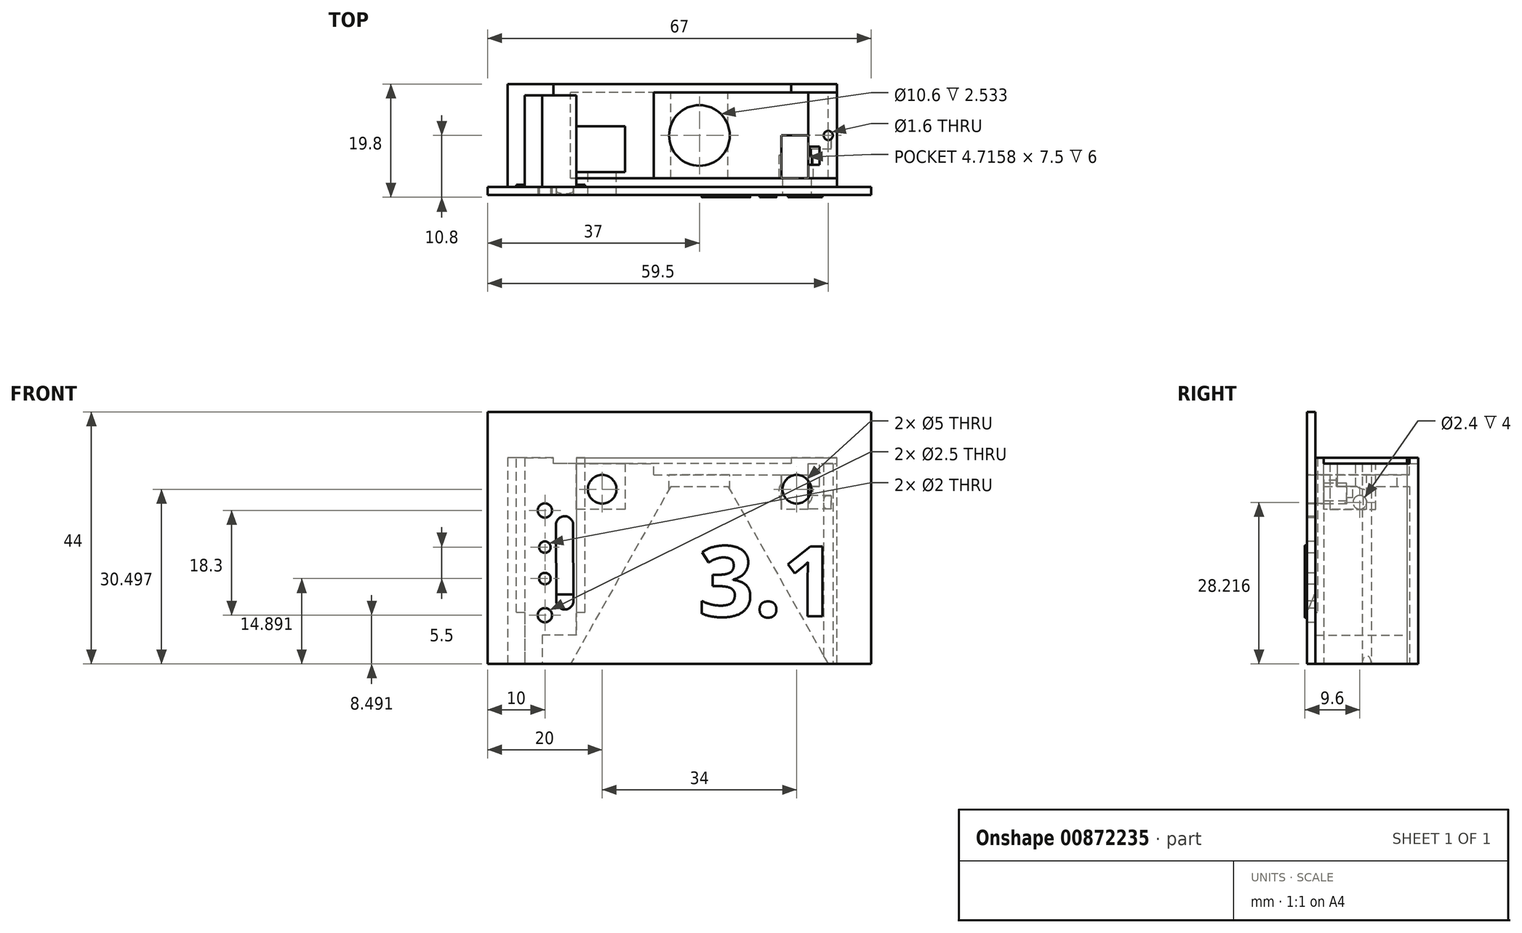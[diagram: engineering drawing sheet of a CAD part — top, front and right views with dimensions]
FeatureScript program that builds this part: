
annotation { "Feature Type Name" : "Feature", "Feature Type Description" : "" }
export const myFeature = defineFeature(function(context is Context, id is Id, definition is map)
    precondition{}
    {
        {
            var Q0;
            Q0=qCreatedBy(makeId("Front.planeOp"),FACE);
            var sketch = newSketch(context, id + "F0", { "sketchPlane" : qUnion([Q0])});
            skLineSegment(sketch, "E0", {"start": v(-6.5, 28.2) * mm, "end": v(6.5, 28.2) * mm});
            skLineSegment(sketch, "E1", {"start": v(-5, 24.2) * mm, "end": v(-22.5, -6.8) * mm});
            skLineSegment(sketch, "E2", {"start": v(5, 24.2) * mm, "end": v(22.5, -6.8) * mm});
            skLineSegment(sketch, "E3", {"start": v(-5, 24.2) * mm, "end": v(5, 24.2) * mm});
            skLineSegment(sketch, "E4", {"start": v(6.5, 24.2) * mm, "end": v(24, -6.8) * mm});
            skLineSegment(sketch, "E5", {"start": v(-24, -6.8) * mm, "end": v(-6.5, 24.2) * mm});
            skLineSegment(sketch, "E6", {"start": v(-24, -6.8) * mm, "end": v(-22.5, -6.8) * mm});
            skLineSegment(sketch, "E7.trimOffspring", {"start": v(22.5, -6.8) * mm, "end": v(24, -6.8) * mm});
            skPoint(sketch, "E8.orphan", {"position": v(-13.41, 24.2) * mm});
            skLineSegment(sketch, "E9", {"start": v(-6.5, 24.2) * mm, "end": v(-6.5, 28.2) * mm});
            skLineSegment(sketch, "E10", {"start": v(6.5, 24.2) * mm, "end": v(6.5, 28.2) * mm});
            skPoint(sketch, "E11.orphan", {"position": v(-7, 28.2) * mm});
            skSolve(sketch);
        }
        {
            var Q0;
            Q0 = qSketchRegion(id + "F0", true);
            extrude(context, id + "F1", {"entities" : qUnion([Q0]), "depth" : 15 * mm, "offsetDistance" : 25 * mm});
        }
        {
            var Q0;
            Q0=makeQuery(id+"F1.opExtrude","SWEPT_FACE",FACE,{"disambiguationData":[OSD([sQuery(id+"F0.wireOp",EDGE,"E9")])]});
            var sketch = newSketch(context, id + "F2", { "sketchPlane" : qUnion([Q0])});
            skLineSegment(sketch, "E12", {"start": v(0, 28.2) * mm, "end": v(15, 28.2) * mm});
            skLineSegment(sketch, "E13", {"start": v(15, 28.2) * mm, "end": v(15, 24.2) * mm});
            skLineSegment(sketch, "E14", {"start": v(15, 24.2) * mm, "end": v(0, 24.2) * mm});
            skLineSegment(sketch, "E15", {"start": v(0, 24.2) * mm, "end": v(0, 28.2) * mm});
            skSolve(sketch);
        }
        {
            var Q0;
            Q0 = qSketchRegion(id + "F2", true);
            extrude(context, id + "F3", {"entities" : qUnion([Q0]), "operationType" : NewBodyOperationType.ADD, "oppositeDirection" : true, "depth" : 25 * mm, "offsetDistance" : 25 * mm, "hasSecondDirection" : true, "secondDirectionOppositeDirection" : false, "secondDirectionDepth" : 1 * mm});
        }
        {
            var Q0;
            Q0=makeQuery(id+"F3.boolean.opBoolean","MERGE",FACE,{"derivedFrom":[makeQuery(id+"F1.opExtrude","SWEPT_FACE",FACE,{"disambiguationData":[OSD([sQuery(id+"F0.wireOp",EDGE,"E0")])]}),makeQuery(id+"F3.opExtrude","SWEPT_FACE",FACE,{"disambiguationData":[OSD([sQuery(id+"F2.wireOp",EDGE,"E12")])]})]});
            var sketch = newSketch(context, id + "F4", { "sketchPlane" : qUnion([Q0])});
            skLineSegment(sketch, "E16", {"start": v(-7.5, -7.5) * mm, "end": v(30.98, -7.5) * mm});
            skCircle(sketch, "E17", {"center": v(0, -7.5) * mm, "radius": 5.3 * mm});
            skSolve(sketch);
        }
        {
            var Q0;
            Q0=makeQuery(id+"F3.boolean.opBoolean","MERGE",FACE,{"derivedFrom":[makeQuery(id+"F1.opExtrude","CAP_FACE",FACE,{"disambiguationData":[OSD([sQuery(id+"F0.wireOp",EDGE,"E0"),sQuery(id+"F0.wireOp",EDGE,"E1"),sQuery(id+"F0.wireOp",EDGE,"E2"),sQuery(id+"F0.wireOp",EDGE,"E3"),sQuery(id+"F0.wireOp",EDGE,"E4"),sQuery(id+"F0.wireOp",EDGE,"E5"),sQuery(id+"F0.wireOp",EDGE,"E6"),sQuery(id+"F0.wireOp",EDGE,"E7.trimOffspring"),sQuery(id+"F0.wireOp",EDGE,"E9"),sQuery(id+"F0.wireOp",EDGE,"E10")])],"isStart":true}),makeQuery(id+"F3.opExtrude","SWEPT_FACE",FACE,{"disambiguationData":[OSD([sQuery(id+"F2.wireOp",EDGE,"E15")])]})]});
            var sketch = newSketch(context, id + "F5", { "sketchPlane" : qUnion([Q0])});
            skLineSegment(sketch, "E18", {"start": v(24, -6.8) * mm, "end": v(24, 28.2) * mm});
            skLineSegment(sketch, "E19", {"start": v(24, 28.2) * mm, "end": v(-24, 28.2) * mm});
            skLineSegment(sketch, "E20", {"start": v(-24, 28.2) * mm, "end": v(-24, -6.8) * mm});
            skLineSegment(sketch, "E21", {"start": v(22.5, -6.8) * mm, "end": v(5, 24.2) * mm});
            skLineSegment(sketch, "E22", {"start": v(5, 24.2) * mm, "end": v(-5, 24.2) * mm});
            skLineSegment(sketch, "E23", {"start": v(-5, 24.2) * mm, "end": v(-22.5, -6.8) * mm});
            skLineSegment(sketch, "E24", {"start": v(-22.5, -6.8) * mm, "end": v(-24, -6.8) * mm});
            skLineSegment(sketch, "E25", {"start": v(22.5, -6.8) * mm, "end": v(24, -6.8) * mm});
            skSolve(sketch);
        }
        {
            var Q0;
            Q0 = qSketchRegion(id + "F4", true);
            extrude(context, id + "F6", {"entities" : qUnion([Q0]), "operationType" : NewBodyOperationType.REMOVE, "oppositeDirection" : true, "depth" : 25 * mm, "offsetDistance" : 25 * mm});
        }
        {
            var Q0;
            Q0 = qSketchRegion(id + "F5", true);
            extrude(context, id + "F7", {"entities" : qUnion([Q0]), "operationType" : NewBodyOperationType.ADD, "oppositeDirection" : true, "depth" : 15 * mm, "offsetDistance" : 25 * mm});
        }
        {
            var Q0;
            Q0=makeQuery(id+"F7.boolean.opBoolean","MERGE",FACE,{"derivedFrom":[makeQuery(id+"F3.boolean.opBoolean","MERGE",FACE,{"derivedFrom":[makeQuery(id+"F1.opExtrude","SWEPT_FACE",FACE,{"disambiguationData":[OSD([sQuery(id+"F0.wireOp",EDGE,"E0")])]}),makeQuery(id+"F3.opExtrude","SWEPT_FACE",FACE,{"disambiguationData":[OSD([sQuery(id+"F2.wireOp",EDGE,"E12")])]})]}),makeQuery(id+"F7.opExtrude","SWEPT_FACE",FACE,{"disambiguationData":[OSD([sQuery(id+"F5.wireOp",EDGE,"E19")])]})]});
            var sketch = newSketch(context, id + "F8", { "sketchPlane" : qUnion([Q0])});
            skLineSegment(sketch, "E26", {"start": v(-27.67, -7.5) * mm, "end": v(34.1, -7.5) * mm});
            skPoint(sketch, "E26.startSnap0", {"position": v(-24, -7.5) * mm});
            skCircle(sketch, "E27", {"center": v(0, -7.5) * mm, "radius": 5.3 * mm});
            skSolve(sketch);
        }
        {
            var Q0;
            Q0 = qSketchRegion(id + "F8", true);
            extrude(context, id + "F9", {"entities" : qUnion([Q0]), "operationType" : NewBodyOperationType.REMOVE, "oppositeDirection" : true, "depth" : 25 * mm, "offsetDistance" : 25 * mm});
        }
        {
            var Q0;
            Q0=makeQuery(id+"F7.boolean.opBoolean","MERGE",FACE,{"derivedFrom":[makeQuery(id+"F3.boolean.opBoolean","MERGE",FACE,{"derivedFrom":[makeQuery(id+"F1.opExtrude","SWEPT_FACE",FACE,{"disambiguationData":[OSD([sQuery(id+"F0.wireOp",EDGE,"E0")])]}),makeQuery(id+"F3.opExtrude","SWEPT_FACE",FACE,{"disambiguationData":[OSD([sQuery(id+"F2.wireOp",EDGE,"E12")])]})]}),makeQuery(id+"F7.opExtrude","SWEPT_FACE",FACE,{"disambiguationData":[OSD([sQuery(id+"F5.wireOp",EDGE,"E19")])]})]});
            var sketch = newSketch(context, id + "F10", { "sketchPlane" : qUnion([Q0])});
            skLineSegment(sketch, "E28", {"start": v(-8, 0) * mm, "end": v(-8, -15) * mm});
            skLineSegment(sketch, "E29", {"start": v(19, 0) * mm, "end": v(19, -15) * mm});
            skLineSegment(sketch, "E30", {"start": v(-8, 0) * mm, "end": v(19, 0) * mm});
            skLineSegment(sketch, "E31", {"start": v(-8, -15) * mm, "end": v(19, -15) * mm});
            skSolve(sketch);
        }
        {
            var Q0;
            Q0 = qSketchRegion(id + "F10", true);
            extrude(context, id + "F11", {"entities" : qUnion([Q0]), "operationType" : NewBodyOperationType.REMOVE, "oppositeDirection" : true, "depth" : 2 * mm, "offsetDistance" : 25 * mm});
        }
        {
            var Q0;
            Q0=makeQuery(id+"F7.boolean.opBoolean","MERGE",FACE,{"derivedFrom":[makeQuery(id+"F3.boolean.opBoolean","MERGE",FACE,{"derivedFrom":[makeQuery(id+"F1.opExtrude","CAP_FACE",FACE,{"disambiguationData":[OSD([sQuery(id+"F0.wireOp",EDGE,"E0"),sQuery(id+"F0.wireOp",EDGE,"E1"),sQuery(id+"F0.wireOp",EDGE,"E2"),sQuery(id+"F0.wireOp",EDGE,"E3"),sQuery(id+"F0.wireOp",EDGE,"E4"),sQuery(id+"F0.wireOp",EDGE,"E5"),sQuery(id+"F0.wireOp",EDGE,"E6"),sQuery(id+"F0.wireOp",EDGE,"E7.trimOffspring"),sQuery(id+"F0.wireOp",EDGE,"E9"),sQuery(id+"F0.wireOp",EDGE,"E10")])],"isStart":true}),makeQuery(id+"F3.opExtrude","SWEPT_FACE",FACE,{"disambiguationData":[OSD([sQuery(id+"F2.wireOp",EDGE,"E15")])]})]}),makeQuery(id+"F7.opExtrude","CAP_FACE",FACE,{"disambiguationData":[OSD([sQuery(id+"F5.wireOp",EDGE,"E18"),sQuery(id+"F5.wireOp",EDGE,"E19"),sQuery(id+"F5.wireOp",EDGE,"E20"),sQuery(id+"F5.wireOp",EDGE,"E21"),sQuery(id+"F5.wireOp",EDGE,"E22"),sQuery(id+"F5.wireOp",EDGE,"E23"),sQuery(id+"F5.wireOp",EDGE,"E24"),sQuery(id+"F5.wireOp",EDGE,"E25")])],"isStart":true})]});
            var sketch = newSketch(context, id + "F12", { "sketchPlane" : qUnion([Q0])});
            skLineSegment(sketch, "E32", {"start": v(-24, 29.2) * mm, "end": v(24, 29.2) * mm});
            skLineSegment(sketch, "E33", {"start": v(-24, -6.8) * mm, "end": v(-24, 29.2) * mm});
            skLineSegment(sketch, "E34", {"start": v(24, -6.8) * mm, "end": v(24, 29.2) * mm});
            skLineSegment(sketch, "E35", {"start": v(-24, -6.8) * mm, "end": v(24, -6.8) * mm});
            skSolve(sketch);
        }
        {
            var Q0;
            Q0 = qSketchRegion(id + "F12", true);
            extrude(context, id + "F13", {"entities" : qUnion([Q0]), "operationType" : NewBodyOperationType.ADD, "depth" : 1.5 * mm, "offsetDistance" : 25 * mm});
        }
        {
            var Q0;
            Q0=makeQuery(id+"F7.boolean.opBoolean","MERGE",FACE,{"derivedFrom":[makeQuery(id+"F3.boolean.opBoolean","MERGE",FACE,{"derivedFrom":[makeQuery(id+"F1.opExtrude","CAP_FACE",FACE,{"disambiguationData":[OSD([sQuery(id+"F0.wireOp",EDGE,"E0"),sQuery(id+"F0.wireOp",EDGE,"E1"),sQuery(id+"F0.wireOp",EDGE,"E2"),sQuery(id+"F0.wireOp",EDGE,"E3"),sQuery(id+"F0.wireOp",EDGE,"E4"),sQuery(id+"F0.wireOp",EDGE,"E5"),sQuery(id+"F0.wireOp",EDGE,"E6"),sQuery(id+"F0.wireOp",EDGE,"E7.trimOffspring"),sQuery(id+"F0.wireOp",EDGE,"E9"),sQuery(id+"F0.wireOp",EDGE,"E10")])],"isStart":false}),makeQuery(id+"F3.opExtrude","SWEPT_FACE",FACE,{"disambiguationData":[OSD([sQuery(id+"F2.wireOp",EDGE,"E13")])]})]}),makeQuery(id+"F7.opExtrude","CAP_FACE",FACE,{"disambiguationData":[OSD([sQuery(id+"F5.wireOp",EDGE,"E18"),sQuery(id+"F5.wireOp",EDGE,"E19"),sQuery(id+"F5.wireOp",EDGE,"E20"),sQuery(id+"F5.wireOp",EDGE,"E21"),sQuery(id+"F5.wireOp",EDGE,"E22"),sQuery(id+"F5.wireOp",EDGE,"E23"),sQuery(id+"F5.wireOp",EDGE,"E24"),sQuery(id+"F5.wireOp",EDGE,"E25")])],"isStart":false})]});
            var sketch = newSketch(context, id + "F14", { "sketchPlane" : qUnion([Q0])});
            skLineSegment(sketch, "E36", {"start": v(-24, 29.2) * mm, "end": v(24, 29.2) * mm});
            skLineSegment(sketch, "E37", {"start": v(-24, -6.8) * mm, "end": v(-24, 29.2) * mm});
            skLineSegment(sketch, "E38", {"start": v(24, -6.8) * mm, "end": v(24, 29.2) * mm});
            skLineSegment(sketch, "E39", {"start": v(-24, -6.8) * mm, "end": v(24, -6.8) * mm});
            skSolve(sketch);
        }
        {
            var Q0;
            Q0 = qSketchRegion(id + "F14", true);
            extrude(context, id + "F15", {"entities" : qUnion([Q0]), "operationType" : NewBodyOperationType.ADD, "depth" : 1.5 * mm, "offsetDistance" : 25 * mm});
        }
        {
            var Q0;
            Q0=makeQuery(id+"F15.opExtrude","CAP_FACE",FACE,{"disambiguationData":[OSD([sQuery(id+"F14.wireOp",EDGE,"E36"),sQuery(id+"F14.wireOp",EDGE,"E37"),sQuery(id+"F14.wireOp",EDGE,"E38"),sQuery(id+"F14.wireOp",EDGE,"E39")])],"isStart":false});
            var sketch = newSketch(context, id + "F16", { "sketchPlane" : qUnion([Q0])});
            skLineSegment(sketch, "E40.0", {"start": v(-30, 37.2) * mm, "end": v(30, 37.2) * mm});
            skLineSegment(sketch, "E41.0", {"start": v(-30, -6.8) * mm, "end": v(-30, 29.2) * mm});
            skLineSegment(sketch, "E41.2", {"start": v(30, -6.8) * mm, "end": v(30, 29.2) * mm});
            skLineSegment(sketch, "E42", {"start": v(-30, -6.8) * mm, "end": v(30, -6.8) * mm});
            skLineSegment(sketch, "E43", {"start": v(30, 29.2) * mm, "end": v(30, 37.2) * mm});
            skLineSegment(sketch, "E44", {"start": v(-30, 29.2) * mm, "end": v(-30, 37.2) * mm});
            skPoint(sketch, "E45.startSnap0", {"position": v(-30, 38.05) * mm});
            skPoint(sketch, "E46.orphan", {"position": v(-30, 37.2) * mm});
            skPoint(sketch, "E47.orphan", {"position": v(-30, 46.9) * mm});
            skPoint(sketch, "E48.orphan", {"position": v(-38.67, 37.2) * mm});
            skPoint(sketch, "E49.orphan", {"position": v(-37.55, -6.8) * mm});
            skSolve(sketch);
        }
        {
            var Q0;
            Q0 = qSketchRegion(id + "F16", true);
            extrude(context, id + "F17", {"entities" : qUnion([Q0]), "operationType" : NewBodyOperationType.ADD, "depth" : 1.4 * mm, "offsetDistance" : 25 * mm});
        }
        {
            var Q0;
            Q0=makeQuery(id+"F15.boolean.opBoolean","MERGE",FACE,{"derivedFrom":[makeQuery(id+"F13.boolean.opBoolean","MERGE",FACE,{"derivedFrom":[makeQuery(id+"F7.opExtrude","SWEPT_FACE",FACE,{"disambiguationData":[OSD([sQuery(id+"F5.wireOp",EDGE,"E18")])]}),makeQuery(id+"F13.opExtrude","SWEPT_FACE",FACE,{"disambiguationData":[OSD([sQuery(id+"F12.wireOp",EDGE,"E34")])]})]}),makeQuery(id+"F15.opExtrude","SWEPT_FACE",FACE,{"disambiguationData":[OSD([sQuery(id+"F14.wireOp",EDGE,"E37")])]})]});
            var sketch = newSketch(context, id + "F18", { "sketchPlane" : qUnion([Q0])});
            skLineSegment(sketch, "E50", {"start": v(5.9, 28.7) * mm, "end": v(5.9, 20.2) * mm});
            skLineSegment(sketch, "E51", {"start": v(5.9, 20.2) * mm, "end": v(13.9, 20.2) * mm});
            skLineSegment(sketch, "E52", {"start": v(13.9, 20.2) * mm, "end": v(13.9, 28.7) * mm});
            skLineSegment(sketch, "E53", {"start": v(13.9, 28.7) * mm, "end": v(5.9, 28.7) * mm});
            skSolve(sketch);
        }
        {
            var Q0;
            Q0 = qSketchRegion(id + "F18", true);
            extrude(context, id + "F19", {"entities" : qUnion([Q0]), "operationType" : NewBodyOperationType.REMOVE, "oppositeDirection" : true, "depth" : 11 * mm, "offsetDistance" : 25 * mm});
        }
        {
            var Q0;
            Q0=makeQuery(id+"F19.boolean.opBoolean","COPY",FACE,{"derivedFrom":makeQuery(id+"F19.opExtrude","SWEPT_FACE",FACE,{"disambiguationData":[OSD([sQuery(id+"F18.wireOp",EDGE,"E52")])]})});
            var sketch = newSketch(context, id + "F20", { "sketchPlane" : qUnion([Q0])});
            skLineSegment(sketch, "E54", {"start": v(19.45, 24.2) * mm, "end": v(14.55, 24.2) * mm});
            skPoint(sketch, "E54.startSnap0", {"position": v(24, 24.2) * mm});
            skLineSegment(sketch, "E55", {"start": v(16.02, 26) * mm, "end": v(17.98, 21.4) * mm});
            skCircle(sketch, "E56", {"center": v(17, 23.7) * mm, "radius": 2.5 * mm});
            skPoint(sketch, "E57.orphan", {"position": v(32.3, 24.2) * mm});
            skPoint(sketch, "E58.orphan", {"position": v(18.5, 20.2) * mm});
            skPoint(sketch, "E59.orphan", {"position": v(15.5, 27.2) * mm});
            skSolve(sketch);
        }
        {
            var Q0;
            Q0 = qSketchRegion(id + "F20", true);
            extrude(context, id + "F21", {"entities" : qUnion([Q0]), "operationType" : NewBodyOperationType.REMOVE, "oppositeDirection" : true, "depth" : 25 * mm, "offsetDistance" : 25 * mm});
        }
        {
            var Q0;
            Q0=makeQuery(id+"F15.boolean.opBoolean","MERGE",FACE,{"derivedFrom":[makeQuery(id+"F13.boolean.opBoolean","MERGE",FACE,{"derivedFrom":[makeQuery(id+"F7.opExtrude","SWEPT_FACE",FACE,{"disambiguationData":[OSD([sQuery(id+"F5.wireOp",EDGE,"E18")])]}),makeQuery(id+"F13.opExtrude","SWEPT_FACE",FACE,{"disambiguationData":[OSD([sQuery(id+"F12.wireOp",EDGE,"E34")])]})]}),makeQuery(id+"F15.opExtrude","SWEPT_FACE",FACE,{"disambiguationData":[OSD([sQuery(id+"F14.wireOp",EDGE,"E37")])]})]});
            var sketch = newSketch(context, id + "F22", { "sketchPlane" : qUnion([Q0])});
            skLineSegment(sketch, "E60", {"start": v(16.5, 29.2) * mm, "end": v(16.5, -6.8) * mm});
            skLineSegment(sketch, "E61", {"start": v(0.5, 29.2) * mm, "end": v(16.5, 29.2) * mm});
            skLineSegment(sketch, "E62", {"start": v(16.5, -1.8) * mm, "end": v(0.5, -1.8) * mm});
            skLineSegment(sketch, "E63", {"start": v(0.5, 29.2) * mm, "end": v(0.5, -1.8) * mm});
            skPoint(sketch, "E64.orphan", {"position": v(0, -1.8) * mm});
            skSolve(sketch);
        }
        {
            var Q0;
            Q0 = qSketchRegion(id + "F22", true);
            extrude(context, id + "F23", {"entities" : qUnion([Q0]), "operationType" : NewBodyOperationType.REMOVE, "oppositeDirection" : true, "depth" : 2.5 * mm, "offsetDistance" : 25 * mm});
        }
        {
            var Q0;
            Q0=makeQuery(id+"F15.boolean.opBoolean","MERGE",FACE,{"derivedFrom":[makeQuery(id+"F13.boolean.opBoolean","MERGE",FACE,{"derivedFrom":[makeQuery(id+"F7.opExtrude","SWEPT_FACE",FACE,{"disambiguationData":[OSD([sQuery(id+"F5.wireOp",EDGE,"E18")])]}),makeQuery(id+"F13.opExtrude","SWEPT_FACE",FACE,{"disambiguationData":[OSD([sQuery(id+"F12.wireOp",EDGE,"E34")])]})]}),makeQuery(id+"F15.opExtrude","SWEPT_FACE",FACE,{"disambiguationData":[OSD([sQuery(id+"F14.wireOp",EDGE,"E37")])]})]});
            var sketch = newSketch(context, id + "F24", { "sketchPlane" : qUnion([Q0])});
            skLineSegment(sketch, "E65", {"start": v(-1.5, 29.2) * mm, "end": v(-1.5, -6.8) * mm});
            skLineSegment(sketch, "E66", {"start": v(-1.5, -6.8) * mm, "end": v(16.5, -6.8) * mm});
            skLineSegment(sketch, "E67", {"start": v(16.5, -6.8) * mm, "end": v(16.5, -1.8) * mm});
            skLineSegment(sketch, "E68", {"start": v(16.5, -1.8) * mm, "end": v(0.5, -1.8) * mm});
            skLineSegment(sketch, "E69", {"start": v(0.5, -1.8) * mm, "end": v(0.5, 28.2) * mm});
            skLineSegment(sketch, "E70", {"start": v(0.5, 28.2) * mm, "end": v(0.5, 29.2) * mm});
            skLineSegment(sketch, "E71", {"start": v(0.5, 29.2) * mm, "end": v(-1.5, 29.2) * mm});
            skSolve(sketch);
        }
        {
            var Q0;
            Q0 = qSketchRegion(id + "F24", true);
            extrude(context, id + "F25", {"entities" : qUnion([Q0]), "operationType" : NewBodyOperationType.ADD, "depth" : 3.5 * mm, "offsetDistance" : 25 * mm});
        }
        {
            var Q0;
            Q0=makeQuery(id+"F25.opExtrude","CAP_FACE",FACE,{"disambiguationData":[OSD([sQuery(id+"F24.wireOp",EDGE,"E65"),sQuery(id+"F24.wireOp",EDGE,"E66"),sQuery(id+"F24.wireOp",EDGE,"E67"),sQuery(id+"F24.wireOp",EDGE,"E68"),sQuery(id+"F24.wireOp",EDGE,"E69"),sQuery(id+"F24.wireOp",EDGE,"E70"),sQuery(id+"F24.wireOp",EDGE,"E71")])],"isStart":false});
            var sketch = newSketch(context, id + "F26", { "sketchPlane" : qUnion([Q0])});
            skLineSegment(sketch, "E72", {"start": v(0.5, 29.2) * mm, "end": v(0.5, -6.8) * mm});
            skLineSegment(sketch, "E73", {"start": v(0.5, -6.8) * mm, "end": v(-1.5, -6.8) * mm});
            skLineSegment(sketch, "E74", {"start": v(-1.5, -6.8) * mm, "end": v(-1.5, 29.2) * mm});
            skLineSegment(sketch, "E75", {"start": v(-1.5, 29.2) * mm, "end": v(0.5, 29.2) * mm});
            skSolve(sketch);
        }
        {
            var Q0;
            Q0 = qSketchRegion(id + "F26", true);
            extrude(context, id + "F27", {"entities" : qUnion([Q0]), "operationType" : NewBodyOperationType.ADD, "depth" : 3 * mm, "offsetDistance" : 25 * mm});
        }
        {
            var Q0;
            Q0=makeQuery(id+"F17.opExtrude","SWEPT_FACE",FACE,{"disambiguationData":[OSD([sQuery(id+"F16.wireOp",EDGE,"E41.0"),sQuery(id+"F16.wireOp",EDGE,"E44")])]});
            var sketch = newSketch(context, id + "F28", { "sketchPlane" : qUnion([Q0])});
            skLineSegment(sketch, "E76", {"start": v(16.5, 37.2) * mm, "end": v(17.9, 37.2) * mm});
            skLineSegment(sketch, "E77", {"start": v(17.9, 37.2) * mm, "end": v(17.9, -6.8) * mm});
            skLineSegment(sketch, "E78", {"start": v(17.9, -6.8) * mm, "end": v(16.5, -6.8) * mm});
            skLineSegment(sketch, "E79", {"start": v(16.5, -6.8) * mm, "end": v(16.5, 37.2) * mm});
            skSolve(sketch);
        }
        {
            var Q0;
            Q0 = qSketchRegion(id + "F28", true);
            extrude(context, id + "F29", {"entities" : qUnion([Q0]), "operationType" : NewBodyOperationType.ADD, "depth" : 7 * mm, "offsetDistance" : 25 * mm});
        }
        {
            var Q0;
            Q0=makeQuery(id+"F27.opExtrude","CAP_FACE",FACE,{"disambiguationData":[OSD([sQuery(id+"F26.wireOp",EDGE,"E72"),sQuery(id+"F26.wireOp",EDGE,"E73"),sQuery(id+"F26.wireOp",EDGE,"E74"),sQuery(id+"F26.wireOp",EDGE,"E75")])],"isStart":false});
            var sketch = newSketch(context, id + "F30", { "sketchPlane" : qUnion([Q0])});
            skLineSegment(sketch, "E80", {"start": v(-1.5, 29.2) * mm, "end": v(17.37, 29.2) * mm});
            skLineSegment(sketch, "E81", {"start": v(-1.5, 29.2) * mm, "end": v(-1.5, -6.8) * mm});
            skLineSegment(sketch, "E82", {"start": v(-1.5, -6.8) * mm, "end": v(17.37, -6.8) * mm});
            skLineSegment(sketch, "E83", {"start": v(17.37, -6.8) * mm, "end": v(17.37, 29.2) * mm});
            skSolve(sketch);
        }
        {
            var Q0;
            Q0 = qSketchRegion(id + "F30", true);
            extrude(context, id + "F31", {"entities" : qUnion([Q0]), "operationType" : NewBodyOperationType.ADD, "depth" : 3 * mm, "offsetDistance" : 25 * mm});
        }
        {
            var Q0;
            Q0=makeQuery(id+"F31.boolean.opBoolean","MERGE",FACE,{"derivedFrom":[makeQuery(id+"F27.boolean.opBoolean","MERGE",FACE,{"derivedFrom":[makeQuery(id+"F25.boolean.opBoolean","MERGE",FACE,{"derivedFrom":[makeQuery(id+"F13.opExtrude","SWEPT_FACE",FACE,{"disambiguationData":[OSD([sQuery(id+"F12.wireOp",EDGE,"E32")])]}),makeQuery(id+"F25.opExtrude","SWEPT_FACE",FACE,{"disambiguationData":[OSD([sQuery(id+"F24.wireOp",EDGE,"E71")])]})]}),makeQuery(id+"F27.opExtrude","SWEPT_FACE",FACE,{"disambiguationData":[OSD([sQuery(id+"F26.wireOp",EDGE,"E75")])]})]}),makeQuery(id+"F31.opExtrude","SWEPT_FACE",FACE,{"disambiguationData":[OSD([sQuery(id+"F30.wireOp",EDGE,"E80")])]})]});
            var sketch = newSketch(context, id + "F32", { "sketchPlane" : qUnion([Q0])});
            skLineSegment(sketch, "E84", {"start": v(-32, -16.5) * mm, "end": v(-20, -16.5) * mm});
            skLineSegment(sketch, "E85", {"start": v(-20, -16.5) * mm, "end": v(-20, -16.1) * mm});
            skLineSegment(sketch, "E86", {"start": v(-20, -16.1) * mm, "end": v(-32, -16.1) * mm});
            skLineSegment(sketch, "E87", {"start": v(-32, -16.1) * mm, "end": v(-32, -16.5) * mm});
            skSolve(sketch);
        }
        {
            var Q0;
            Q0 = qSketchRegion(id + "F32", true);
            extrude(context, id + "F33", {"entities" : qUnion([Q0]), "operationType" : NewBodyOperationType.REMOVE, "oppositeDirection" : true, "depth" : 27 * mm, "offsetDistance" : 25 * mm});
        }
        {
            var Q0;
            Q0=makeQuery(id+"F29.boolean.opBoolean","MERGE",FACE,{"derivedFrom":[makeQuery(id+"F17.opExtrude","CAP_FACE",FACE,{"disambiguationData":[OSD([sQuery(id+"F16.wireOp",EDGE,"E41.0"),sQuery(id+"F16.wireOp",EDGE,"E41.2"),sQuery(id+"F16.wireOp",EDGE,"E42"),sQuery(id+"F16.wireOp",EDGE,"E43"),sQuery(id+"F16.wireOp",EDGE,"E44"),sQuery(id+"F16.wireOp",EDGE,"E40.0")])],"isStart":false}),makeQuery(id+"F29.opExtrude","SWEPT_FACE",FACE,{"disambiguationData":[OSD([sQuery(id+"F28.wireOp",EDGE,"E77")])]})]});
            var sketch = newSketch(context, id + "F34", { "sketchPlane" : qUnion([Q0])});
            skLineSegment(sketch, "E88", {"start": v(-27, 27.43) * mm, "end": v(-27, -0.23) * mm});
            skCircle(sketch, "E89", {"center": v(-27, 20) * mm, "radius": 1.25 * mm});
            skCircle(sketch, "E90", {"center": v(-27, 13.6) * mm, "radius": 1 * mm});
            skArc(sketch, "E91", {"start": v(-25, 10.65) * mm, "mid": v(-25, 10.61) * mm, "end": v(-25, 10.57) * mm});
            skCircle(sketch, "E92", {"center": v(-27, 8.1) * mm, "radius": 1 * mm});
            skArc(sketch, "E93", {"start": v(-25, 4.21) * mm, "mid": v(-23.5, 2.7) * mm, "end": v(-22, 4.21) * mm});
            skCircle(sketch, "E94", {"center": v(-27, 1.7) * mm, "radius": 1.25 * mm});
            skArc(sketch, "E95", {"start": v(-22.06, 17.5) * mm, "mid": v(-23.56, 19) * mm, "end": v(-25.06, 17.49) * mm});
            skLineSegment(sketch, "E96", {"start": v(-25.06, 17.5) * mm, "end": v(-25, 4.21) * mm});
            skLineSegment(sketch, "E97", {"start": v(-22.06, 17.5) * mm, "end": v(-22, 4.21) * mm});
            skPoint(sketch, "E98.start.orphan", {"position": v(-26.31, 17.5) * mm});
            skSolve(sketch);
        }
        {
            var Q0;
            Q0 = qSketchRegion(id + "F34", true);
            extrude(context, id + "F35", {"entities" : qUnion([Q0]), "operationType" : NewBodyOperationType.REMOVE, "oppositeDirection" : true, "depth" : 3 * mm, "offsetDistance" : 25 * mm});
        }
        {
            var Q0;
            Q0=makeQuery(id+"F29.boolean.opBoolean","MERGE",FACE,{"derivedFrom":[makeQuery(id+"F17.opExtrude","CAP_FACE",FACE,{"disambiguationData":[OSD([sQuery(id+"F16.wireOp",EDGE,"E41.0"),sQuery(id+"F16.wireOp",EDGE,"E41.2"),sQuery(id+"F16.wireOp",EDGE,"E42"),sQuery(id+"F16.wireOp",EDGE,"E43"),sQuery(id+"F16.wireOp",EDGE,"E44"),sQuery(id+"F16.wireOp",EDGE,"E40.0")])],"isStart":false}),makeQuery(id+"F29.opExtrude","SWEPT_FACE",FACE,{"disambiguationData":[OSD([sQuery(id+"F28.wireOp",EDGE,"E77")])]})]});
            var sketch = newSketch(context, id + "F36", { "sketchPlane" : qUnion([Q0])});
            skText(sketch, "E99", { "text": "3.1", "fontName": "OpenSans-Bold.ttf"});
            const initialGuessF36  = {"E99": [-0.00023, 0.0015, 1, 0, 0.01232]};
            skSetInitialGuess(sketch, initialGuessF36);
            skSolve(sketch);
        }
        {
            var Q0;
            Q0 = qSketchRegion(id + "F36", true);
            extrude(context, id + "F37", {"entities" : qUnion([Q0]), "operationType" : NewBodyOperationType.ADD, "depth" : .4 * mm, "offsetDistance" : 25 * mm});
        }
        {
            var Q0;
            Q0=makeQuery(id+"F35.boolean.opBoolean","COPY",FACE,{"derivedFrom":makeQuery(id+"F35.opExtrude","SWEPT_FACE",FACE,{"disambiguationData":[OSD([sQuery(id+"F34.wireOp",EDGE,"E96")])]})});
            var sketch = newSketch(context, id + "F38", { "sketchPlane" : qUnion([Q0])});
            skLineSegment(sketch, "E100", {"start": v(-17.9, 2.32) * mm, "end": v(-16.5, 2.32) * mm});
            skLineSegment(sketch, "E101", {"start": v(-16.7, 5.35) * mm, "end": v(-17.9, 2.32) * mm});
            skLineSegment(sketch, "E102", {"start": v(-16.5, 5.32) * mm, "end": v(-16.5, 2.32) * mm});
            skPoint(sketch, "E103.visualSharp", {"position": v(-16.5, 5.84) * mm});
            skArc(sketch, "E103.filletArc", {"start": v(-16.6, 5.42) * mm, "mid": v(-16.65, 5.4) * mm, "end": v(-16.7, 5.35) * mm});
            skPoint(sketch, "E104.orphan", {"position": v(-15.53, 2.32) * mm});
            skLineSegment(sketch, "E105", {"start": v(-16.5, 5.32) * mm, "end": v(-16.5, 5.41) * mm});
            skLineSegment(sketch, "E106", {"start": v(-16.6, 5.42) * mm, "end": v(-16.5, 5.41) * mm});
            skSolve(sketch);
        }
        {
            var Q0;
            {var subQ9=sQuery(id+"F0.wireOp",EDGE,"E0");var subQ15=sQuery(id+"F5.wireOp",EDGE,"E20");var subQ16=sQuery(id+"F5.wireOp",EDGE,"E19");Q0=makeQuery(id+"F11.boolean.opBoolean","SPLIT",FACE,{"disambiguationData":[TD([makeQuery(id+"F7.opExtrude","SWEPT_FACE",FACE,{"disambiguationData":[OSD([subQ15])]})])],"derivedFrom":makeQuery(id+"F7.boolean.opBoolean","MERGE",FACE,{"derivedFrom":[makeQuery(id+"F3.boolean.opBoolean","MERGE",FACE,{"derivedFrom":[makeQuery(id+"F1.opExtrude","SWEPT_FACE",FACE,{"disambiguationData":[OSD([subQ9])]}),makeQuery(id+"F3.opExtrude","SWEPT_FACE",FACE,{"disambiguationData":[OSD([sQuery(id+"F2.wireOp",EDGE,"E12")])]})]}),makeQuery(id+"F7.opExtrude","SWEPT_FACE",FACE,{"disambiguationData":[OSD([subQ16])]})]})});}
            var sketch = newSketch(context, id + "F39", { "sketchPlane" : qUnion([Q0])});
            skLineSegment(sketch, "E107", {"start": v(19, -15) * mm, "end": v(14.28, -15) * mm});
            skLineSegment(sketch, "E108", {"start": v(14.28, -15) * mm, "end": v(14.28, 0) * mm});
            skLineSegment(sketch, "E109", {"start": v(14.28, 0) * mm, "end": v(19, 0) * mm});
            skLineSegment(sketch, "E110", {"start": v(19, 0) * mm, "end": v(19, -15) * mm});
            skSolve(sketch);
        }
        {
            var Q0;
            Q0 = qSketchRegion(id + "F39", true);
            extrude(context, id + "F40", {"entities" : qUnion([Q0]), "operationType" : NewBodyOperationType.REMOVE, "oppositeDirection" : true, "depth" : 8 * mm, "offsetDistance" : 25 * mm});
        }
        {
            var Q0;
            Q0 = qSketchRegion(id + "F38", true);
            extrude(context, id + "F41", {"entities" : qUnion([Q0]), "operationType" : NewBodyOperationType.ADD, "depth" : 25 * mm, "offsetDistance" : 25 * mm});
        }
        {
            var Q0;
            Q0=makeQuery(id+"F29.boolean.opBoolean","MERGE",FACE,{"derivedFrom":[makeQuery(id+"F17.opExtrude","CAP_FACE",FACE,{"disambiguationData":[OSD([sQuery(id+"F16.wireOp",EDGE,"E41.0"),sQuery(id+"F16.wireOp",EDGE,"E41.2"),sQuery(id+"F16.wireOp",EDGE,"E42"),sQuery(id+"F16.wireOp",EDGE,"E43"),sQuery(id+"F16.wireOp",EDGE,"E44"),sQuery(id+"F16.wireOp",EDGE,"E40.0")])],"isStart":false}),makeQuery(id+"F29.opExtrude","SWEPT_FACE",FACE,{"disambiguationData":[OSD([sQuery(id+"F28.wireOp",EDGE,"E77")])]})]});
            var sketch = newSketch(context, id + "F42", { "sketchPlane" : qUnion([Q0])});
            skCircle(sketch, "E111", {"center": v(17, 23.7) * mm, "radius": 2.5 * mm});
            skSolve(sketch);
        }
        {
            var Q0;
            Q0 = qSketchRegion(id + "F42", true);
            extrude(context, id + "F43", {"entities" : qUnion([Q0]), "operationType" : NewBodyOperationType.REMOVE, "oppositeDirection" : true, "depth" : 8 * mm, "offsetDistance" : 25 * mm});
        }
        {
            var Q0;
            {var subQ2=sQuery(id+"F14.wireOp",EDGE,"E36");var subQ3=sQuery(id+"F14.wireOp",EDGE,"E37");var subQ4=sQuery(id+"F14.wireOp",EDGE,"E38");Q0=makeQuery(id+"F40.boolean.opBoolean","MERGE",FACE,{"derivedFrom":[makeQuery(id+"F15.boolean.opBoolean","SPLIT",FACE,{"disambiguationData":[TD([makeQuery(id+"F1.opExtrude","SWEPT_FACE",FACE,{"disambiguationData":[OSD([sQuery(id+"F0.wireOp",EDGE,"E0")])]})])],"derivedFrom":makeQuery(id+"F15.opExtrude","CAP_FACE",FACE,{"disambiguationData":[OSD([subQ2,subQ3,subQ4,sQuery(id+"F14.wireOp",EDGE,"E39")])],"isStart":true})})],"fromTools":[makeQuery(id+"F40.opExtrude","SWEPT_FACE",FACE,{"disambiguationData":[OSD([sQuery(id+"F39.wireOp",EDGE,"E107")])]})]});}
            var sketch = newSketch(context, id + "F44", { "sketchPlane" : qUnion([Q0])});
            skLineSegment(sketch, "E112", {"start": v(-14.5, 23.7) * mm, "end": v(-22.12, 23.7) * mm});
            skLineSegment(sketch, "E113", {"start": v(-14.28, 23.2) * mm, "end": v(-20.17, 23.2) * mm});
            skCircle(sketch, "E114", {"center": v(-16.83, 23.2) * mm, "radius": 3 * mm});
            skSolve(sketch);
        }
        {
            var Q0;
            Q0 = qSketchRegion(id + "F44", true);
            extrude(context, id + "F45", {"entities" : qUnion([Q0]), "operationType" : NewBodyOperationType.REMOVE, "depth" : 4 * mm, "offsetDistance" : 25 * mm});
        }
        {
            var Q0;
            Q0=makeQuery(id+"F11.boolean.opBoolean","COPY",FACE,{"derivedFrom":makeQuery(id+"F11.opExtrude","CAP_FACE",FACE,{"disambiguationData":[OSD([sQuery(id+"F10.wireOp",EDGE,"E28"),sQuery(id+"F10.wireOp",EDGE,"E29"),sQuery(id+"F10.wireOp",EDGE,"E30"),sQuery(id+"F10.wireOp",EDGE,"E31")])],"isStart":false})});
            var sketch = newSketch(context, id + "F46", { "sketchPlane" : qUnion([Q0])});
            skLineSegment(sketch, "E115", {"start": v(14.28, -7.5) * mm, "end": v(20.07, -7.5) * mm});
            skLineSegment(sketch, "E116", {"start": v(20.07, -7.5) * mm, "end": v(20.07, 0.68) * mm});
            skLineSegment(sketch, "E117", {"start": v(20.07, 0.68) * mm, "end": v(13.38, 0.68) * mm});
            skLineSegment(sketch, "E118", {"start": v(13.38, 0.68) * mm, "end": v(13.38, -7.5) * mm});
            skLineSegment(sketch, "E119", {"start": v(13.38, -7.5) * mm, "end": v(14.28, -7.5) * mm});
            skSolve(sketch);
        }
        {
            var Q0;
            Q0 = qSketchRegion(id + "F46", true);
            extrude(context, id + "F47", {"entities" : qUnion([Q0]), "operationType" : NewBodyOperationType.ADD, "oppositeDirection" : true, "depth" : 6.5 * mm, "offsetDistance" : 25 * mm});
        }
        {
            var Q0;
            Q0=makeQuery(id+"F31.boolean.opBoolean","MERGE",FACE,{"derivedFrom":[makeQuery(id+"F27.boolean.opBoolean","MERGE",FACE,{"derivedFrom":[makeQuery(id+"F25.boolean.opBoolean","MERGE",FACE,{"derivedFrom":[makeQuery(id+"F13.opExtrude","CAP_FACE",FACE,{"disambiguationData":[OSD([sQuery(id+"F12.wireOp",EDGE,"E32"),sQuery(id+"F12.wireOp",EDGE,"E33"),sQuery(id+"F12.wireOp",EDGE,"E34"),sQuery(id+"F12.wireOp",EDGE,"E35")])],"isStart":false}),makeQuery(id+"F25.opExtrude","SWEPT_FACE",FACE,{"disambiguationData":[OSD([sQuery(id+"F24.wireOp",EDGE,"E65")])]})]}),makeQuery(id+"F27.opExtrude","SWEPT_FACE",FACE,{"disambiguationData":[OSD([sQuery(id+"F26.wireOp",EDGE,"E74")])]})]}),makeQuery(id+"F31.opExtrude","SWEPT_FACE",FACE,{"disambiguationData":[OSD([sQuery(id+"F30.wireOp",EDGE,"E81")])]})]});
            var sketch = newSketch(context, id + "F48", { "sketchPlane" : qUnion([Q0])});
            skLineSegment(sketch, "E120", {"start": v(-16, 29.2) * mm, "end": v(-16, 28.2) * mm});
            skLineSegment(sketch, "E121", {"start": v(-16, 28.2) * mm, "end": v(25.5, 28.2) * mm});
            skLineSegment(sketch, "E122", {"start": v(25.5, 28.2) * mm, "end": v(25.5, 29.2) * mm});
            skLineSegment(sketch, "E123", {"start": v(25.5, 29.2) * mm, "end": v(-16, 29.2) * mm});
            skSolve(sketch);
        }
        {
            var Q0;
            Q0 = qSketchRegion(id + "F48", true);
            extrude(context, id + "F49", {"entities" : qUnion([Q0]), "operationType" : NewBodyOperationType.REMOVE, "oppositeDirection" : true, "depth" : 2 * mm, "offsetDistance" : 25 * mm});
        }
        {
            var Q0;
            {var subQ9=sQuery(id+"F0.wireOp",EDGE,"E0");var subQ15=sQuery(id+"F5.wireOp",EDGE,"E20");var subQ16=sQuery(id+"F5.wireOp",EDGE,"E19");Q0=makeQuery(id+"F11.boolean.opBoolean","SPLIT",FACE,{"disambiguationData":[TD([makeQuery(id+"F7.opExtrude","SWEPT_FACE",FACE,{"disambiguationData":[OSD([subQ15])]})])],"derivedFrom":makeQuery(id+"F7.boolean.opBoolean","MERGE",FACE,{"derivedFrom":[makeQuery(id+"F3.boolean.opBoolean","MERGE",FACE,{"derivedFrom":[makeQuery(id+"F1.opExtrude","SWEPT_FACE",FACE,{"disambiguationData":[OSD([subQ9])]}),makeQuery(id+"F3.opExtrude","SWEPT_FACE",FACE,{"disambiguationData":[OSD([sQuery(id+"F2.wireOp",EDGE,"E12")])]})]}),makeQuery(id+"F7.opExtrude","SWEPT_FACE",FACE,{"disambiguationData":[OSD([subQ16])]})]})});}
            var sketch = newSketch(context, id + "F50", { "sketchPlane" : qUnion([Q0])});
            skLineSegment(sketch, "E124", {"start": v(19, -12.6) * mm, "end": v(21, -12.6) * mm});
            skLineSegment(sketch, "E125", {"start": v(21, -12.6) * mm, "end": v(21, -9.42) * mm});
            skLineSegment(sketch, "E126", {"start": v(21, -9.42) * mm, "end": v(19, -9.42) * mm});
            skLineSegment(sketch, "E127", {"start": v(19, -9.42) * mm, "end": v(19, -12.6) * mm});
            skSolve(sketch);
        }
        {
            var Q0;
            Q0 = qSketchRegion(id + "F50", true);
            extrude(context, id + "F51", {"entities" : qUnion([Q0]), "operationType" : NewBodyOperationType.REMOVE, "oppositeDirection" : true, "depth" : 4 * mm, "offsetDistance" : 25 * mm});
        }
        {
            var Q0;
            Q0=makeQuery(id+"F31.boolean.opBoolean","MERGE",FACE,{"derivedFrom":[makeQuery(id+"F29.boolean.opBoolean","MERGE",FACE,{"derivedFrom":[makeQuery(id+"F27.boolean.opBoolean","MERGE",FACE,{"derivedFrom":[makeQuery(id+"F25.boolean.opBoolean","MERGE",FACE,{"derivedFrom":[makeQuery(id+"F17.boolean.opBoolean","MERGE",FACE,{"derivedFrom":[makeQuery(id+"F15.boolean.opBoolean","MERGE",FACE,{"derivedFrom":[makeQuery(id+"F13.boolean.opBoolean","MERGE",FACE,{"derivedFrom":[makeQuery(id+"F1.opExtrude","SWEPT_FACE",FACE,{"disambiguationData":[OSD([sQuery(id+"F0.wireOp",EDGE,"E6")])]}),makeQuery(id+"F1.opExtrude","SWEPT_FACE",FACE,{"disambiguationData":[OSD([sQuery(id+"F0.wireOp",EDGE,"E7.trimOffspring")])]}),makeQuery(id+"F13.opExtrude","SWEPT_FACE",FACE,{"disambiguationData":[OSD([sQuery(id+"F12.wireOp",EDGE,"E35")])]})]}),makeQuery(id+"F15.opExtrude","SWEPT_FACE",FACE,{"disambiguationData":[OSD([sQuery(id+"F14.wireOp",EDGE,"E39")])]})]}),makeQuery(id+"F17.opExtrude","SWEPT_FACE",FACE,{"disambiguationData":[OSD([sQuery(id+"F16.wireOp",EDGE,"E42")])]})]}),makeQuery(id+"F25.opExtrude","SWEPT_FACE",FACE,{"disambiguationData":[OSD([sQuery(id+"F24.wireOp",EDGE,"E66")])]})]}),makeQuery(id+"F27.opExtrude","SWEPT_FACE",FACE,{"disambiguationData":[OSD([sQuery(id+"F26.wireOp",EDGE,"E73")])]})]}),makeQuery(id+"F29.opExtrude","SWEPT_FACE",FACE,{"disambiguationData":[OSD([sQuery(id+"F28.wireOp",EDGE,"E78")])]})]}),makeQuery(id+"F31.opExtrude","SWEPT_FACE",FACE,{"disambiguationData":[OSD([sQuery(id+"F30.wireOp",EDGE,"E82")])]})]});
            var sketch = newSketch(context, id + "F52", { "sketchPlane" : qUnion([Q0])});
            skCircle(sketch, "E128", {"center": v(22.5, 7.5) * mm, "radius": 0.8 * mm});
            skSolve(sketch);
        }
        {
            var Q0;
            Q0 = qSketchRegion(id + "F52", true);
            extrude(context, id + "F53", {"entities" : qUnion([Q0]), "operationType" : NewBodyOperationType.REMOVE, "oppositeDirection" : true, "depth" : 40 * mm, "offsetDistance" : 25 * mm});
        }
        {
            var Q0;
            {var subQ0=sQuery(id+"F10.wireOp",EDGE,"E29");var subQ1=makeQuery(id+"F11.boolean.opBoolean","COPY",FACE,{"derivedFrom":makeQuery(id+"F11.opExtrude","SWEPT_FACE",FACE,{"disambiguationData":[OSD([subQ0])]})});var subQ8=sQuery(id+"F42.wireOp",EDGE,"E111");var subQ9=makeQuery(id+"F43.boolean.opBoolean","COPY",FACE,{"derivedFrom":makeQuery(id+"F43.opExtrude","SWEPT_FACE",FACE,{"disambiguationData":[OSD([subQ8])]})});var subQ11=sQuery(id+"F39.wireOp",EDGE,"E110");Q0=makeQuery(id+"F51.boolean.opBoolean","SPLIT",FACE,{"disambiguationData":[TD([subQ9])],"derivedFrom":makeQuery(id+"F40.boolean.opBoolean","MERGE",FACE,{"derivedFrom":[subQ1],"fromTools":[makeQuery(id+"F40.opExtrude","SWEPT_FACE",FACE,{"disambiguationData":[OSD([subQ11])]})]})});}
            var sketch = newSketch(context, id + "F54", { "sketchPlane" : qUnion([Q0])});
            skCircle(sketch, "E129", {"center": v(8.7, 21.43) * mm, "radius": 1.2 * mm});
            skSolve(sketch);
        }
        {
            var Q0;
            Q0 = qSketchRegion(id + "F54", true);
            extrude(context, id + "F55", {"entities" : qUnion([Q0]), "operationType" : NewBodyOperationType.REMOVE, "oppositeDirection" : true, "depth" : 4 * mm, "offsetDistance" : 25 * mm});
        }
    });
